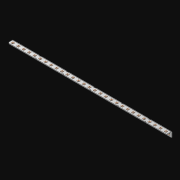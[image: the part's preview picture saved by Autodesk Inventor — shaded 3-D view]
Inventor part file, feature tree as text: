
AUTODESK INVENTOR PART (.ipt)
format: ipt  version: 2021 (Build 250183000, 183)  size: 812,032 bytes
history: native  units: in
note: dims shown in document units (in); Inventor stores cm internally (conversion verified against a paired STEP export)
features: extrude x59, other x58, sketch x3, pattern_linear x1, sheet_metal_op x1
ambient origin geometry x8: Origin, YZ Plane, XZ Plane, XY Plane, X Axis, Y Axis, Z Axis, Center Point
bodies: Solid1 (feature_tree)
feature tree (122):
  pattern_linear  "Rectangular Pattern1"  Spacing1=0.063in  [1 undecoded]
  extrude  "Extrusion1"  Depth=0.5in
  sketch  "Sketch1"  dims[d0=0.182in]
  other  "Srf1"
  sketch  "Sketch2"  dims[d1=0.063in d2=0.0in]
  other  "Srf2"
  other  "Srf3"
  other  "Srf5"
  other  "Srf7"
  other  "Srf9"
  other  "Srf11"
  other  "Srf13"
  other  "Srf15"
  other  "Srf17"
  other  "Srf19"
  other  "Srf21"
  other  "Srf23"
  other  "Srf25"
  other  "Srf27"
  other  "Srf29"
  other  "Srf31"
  other  "Srf33"
  other  "Srf35"
  other  "Srf37"
  other  "Srf39"
  other  "Srf41"
  other  "Srf43"
  other  "Srf45"
  other  "Srf47"
  other  "Srf49"
  other  "Srf51"
  other  "Srf53"
  other  "Srf55"
  other  "Srf57"
  other  "Srf4"
  other  "Srf6"
  other  "Srf8"
  other  "Srf10"
  other  "Srf12"
  other  "Srf14"
  other  "Srf16"
  other  "Srf18"
  other  "Srf20"
  other  "Srf22"
  other  "Srf24"
  other  "Srf26"
  other  "Srf28"
  other  "Srf30"
  other  "Srf32"
  other  "Srf34"
  other  "Srf36"
  other  "Srf38"
  other  "Srf40"
  other  "Srf42"
  other  "Srf44"
  other  "Srf46"
  other  "Srf48"
  other  "Srf50"
  other  "Srf52"
  other  "Srf54"
  other  "Srf56"
  other  "Srf58"
  sketch  "Sketch3"  dims[d3=0.182in d4=0.063in d5=0.0in d8=0.5in d9=3.0in d10=0.0in]
  sheet_metal_op  "Fold1"
  extrude  "ExtrusionSrf1"  Depth=0.5in TaperAngle=0.0deg
  extrude  "ExtrusionSrf2"  [1 undecoded]
  extrude  "ExtrusionSrf3"  [1 undecoded]
  extrude  "ExtrusionSrf4"  [1 undecoded]
  extrude  "ExtrusionSrf5"  [1 undecoded]
  extrude  "ExtrusionSrf6"  [1 undecoded]
  extrude  "ExtrusionSrf7"  [1 undecoded]
  extrude  "ExtrusionSrf8"  [1 undecoded]
  extrude  "ExtrusionSrf9"  [1 undecoded]
  extrude  "ExtrusionSrf10"  [1 undecoded]
  extrude  "ExtrusionSrf11"  [1 undecoded]
  extrude  "ExtrusionSrf12"  [1 undecoded]
  extrude  "ExtrusionSrf13"  [1 undecoded]
  extrude  "ExtrusionSrf14"  [1 undecoded]
  extrude  "ExtrusionSrf15"  [1 undecoded]
  extrude  "ExtrusionSrf16"  [1 undecoded]
  extrude  "ExtrusionSrf17"  [1 undecoded]
  extrude  "ExtrusionSrf18"  [1 undecoded]
  extrude  "ExtrusionSrf19"  [1 undecoded]
  extrude  "ExtrusionSrf20"  [1 undecoded]
  extrude  "ExtrusionSrf21"  [1 undecoded]
  extrude  "ExtrusionSrf22"  [1 undecoded]
  extrude  "ExtrusionSrf23"  [1 undecoded]
  extrude  "ExtrusionSrf24"  [1 undecoded]
  extrude  "ExtrusionSrf25"  [1 undecoded]
  extrude  "ExtrusionSrf26"  [1 undecoded]
  extrude  "ExtrusionSrf27"  [1 undecoded]
  extrude  "ExtrusionSrf28"  [1 undecoded]
  extrude  "ExtrusionSrf29"  [1 undecoded]
  extrude  "ExtrusionSrf30"  [1 undecoded]
  extrude  "ExtrusionSrf37"  [1 undecoded]
  extrude  "ExtrusionSrf38"  [1 undecoded]
  extrude  "ExtrusionSrf39"  [1 undecoded]
  extrude  "ExtrusionSrf40"  [1 undecoded]
  extrude  "ExtrusionSrf41"  [1 undecoded]
  extrude  "ExtrusionSrf42"  [1 undecoded]
  extrude  "ExtrusionSrf43"  [1 undecoded]
  extrude  "ExtrusionSrf44"  [1 undecoded]
  extrude  "ExtrusionSrf45"  [1 undecoded]
  extrude  "ExtrusionSrf46"  [1 undecoded]
  extrude  "ExtrusionSrf47"  [1 undecoded]
  extrude  "ExtrusionSrf48"  [1 undecoded]
  extrude  "ExtrusionSrf49"  [1 undecoded]
  extrude  "ExtrusionSrf50"  [1 undecoded]
  extrude  "ExtrusionSrf51"  [1 undecoded]
  extrude  "ExtrusionSrf52"  [1 undecoded]
  extrude  "ExtrusionSrf53"  [1 undecoded]
  extrude  "ExtrusionSrf54"  [1 undecoded]
  extrude  "ExtrusionSrf55"  [1 undecoded]
  extrude  "ExtrusionSrf56"  [1 undecoded]
  extrude  "ExtrusionSrf57"  [1 undecoded]
  extrude  "ExtrusionSrf58"  [1 undecoded]
  extrude  "ExtrusionSrf59"  [1 undecoded]
  extrude  "ExtrusionSrf60"  [1 undecoded]
  extrude  "ExtrusionSrf61"  [1 undecoded]
  extrude  "ExtrusionSrf62"  [1 undecoded]
  extrude  "ExtrusionSrf63"  [1 undecoded]
  extrude  "ExtrusionSrf64"  [1 undecoded]
note: 58 required parameter values undecoded (feature->parameter linkage not recoverable at this tier; creation-order binding heuristic only, values carry confidence <= 0.55)
